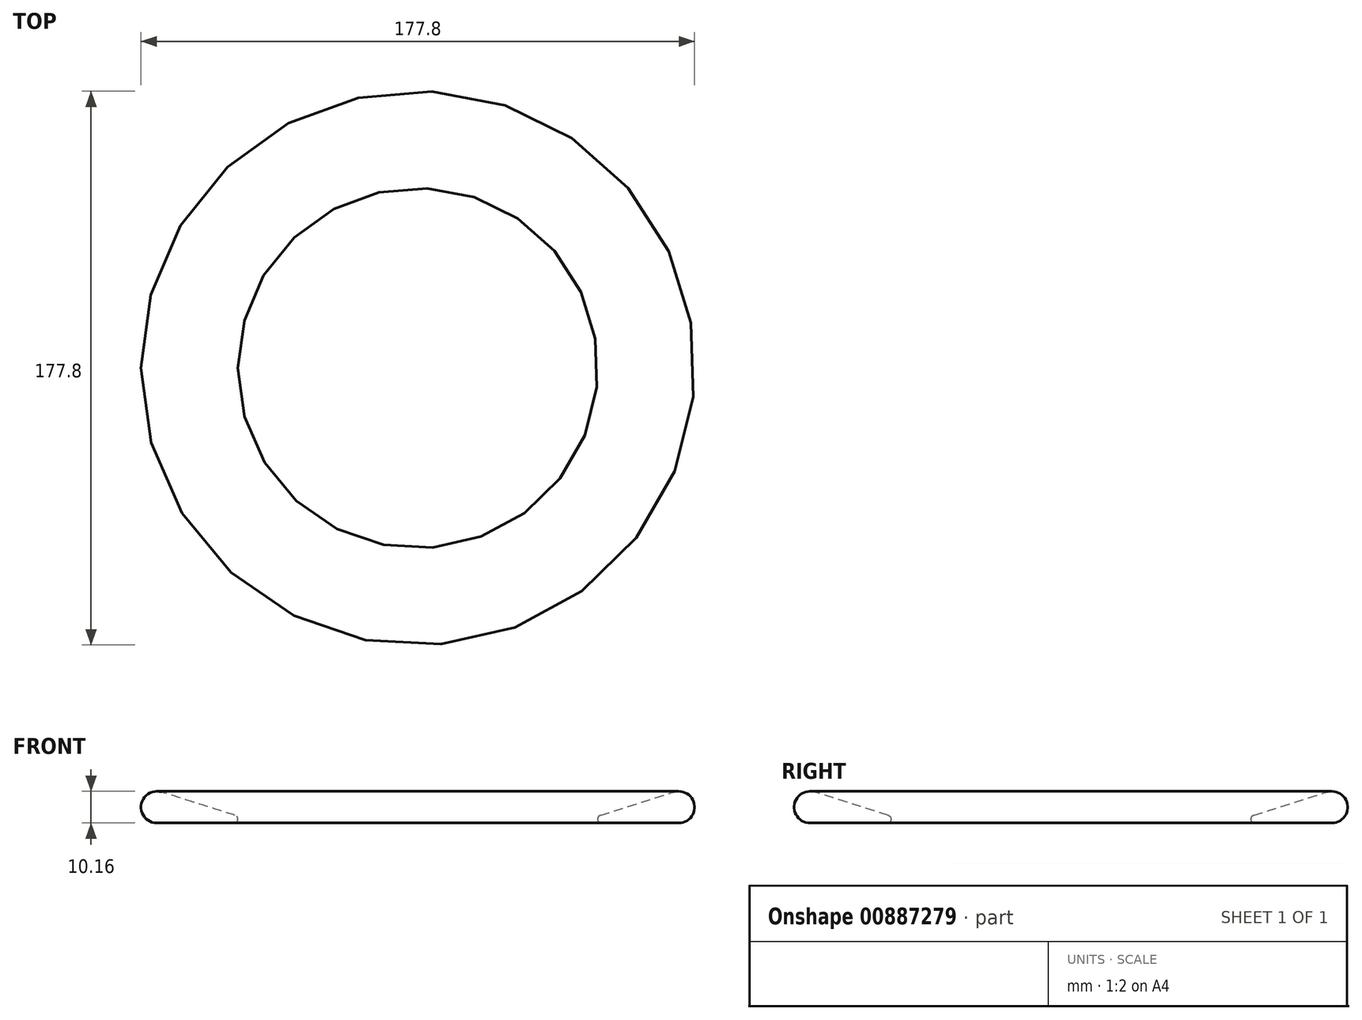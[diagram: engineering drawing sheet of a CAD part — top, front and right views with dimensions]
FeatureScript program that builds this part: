
annotation { "Feature Type Name" : "Feature", "Feature Type Description" : "" }
export const myFeature = defineFeature(function(context is Context, id is Id, definition is map)
    precondition{}
    {
        {
            var Q0;
            Q0=qCreatedBy(makeId("Front.planeOp"),FACE);
            var sketch = newSketch(context, id + "F0", { "sketchPlane" : qUnion([Q0])});
            skLineSegment(sketch, "E0", {"start": v(0, 0) * mm, "end": v(-50.8, 0) * mm});
            skLineSegment(sketch, "E1", {"start": v(-59.06, 0) * mm, "end": v(-83.82, 0) * mm});
            skArc(sketch, "E2", {"start": v(-83.82, 0) * mm, "mid": v(-88.84, 5.85) * mm, "end": v(-82.3, 9.93) * mm});
            skLineSegment(sketch, "E3", {"start": v(-82.3, 9.93) * mm, "end": v(-58.67, 2.48) * mm});
            skLineSegment(sketch, "E4", {"start": v(-88.9, 10.16) * mm, "end": v(-83.82, 10.16) * mm});
            skLineSegment(sketch, "E5", {"start": v(-88.9, 5.08) * mm, "end": v(-88.9, 0) * mm});
            skLineSegment(sketch, "E6", {"start": v(0, 0) * mm, "end": v(50.8, 0) * mm});
            skLineSegment(sketch, "E7", {"start": v(0, 0) * mm, "end": v(0, 40.2) * mm});
            skPoint(sketch, "E8.visualSharp", {"position": v(-50.8, 0) * mm});
            skArc(sketch, "E8.filletArc", {"start": v(-59.06, 0) * mm, "mid": v(-57.8, 1.08) * mm, "end": v(-58.67, 2.48) * mm});
            skSolve(sketch);
        }
        {
            var Q0;
            {var subQ4=sQuery(id+"F0.wireOp",EDGE,"E1");Q0=makeQuery(id+"F0.imprint","IMPRINT",FACE,{"disambiguationData":[TD([[makeQuery(id+"F0.imprint","IMPRINT",EDGE,{"derivedFrom":subQ4}),-1.0]])]});}
            var Q1;
            Q1=sQuery(id+"F0.wireOp",EDGE,"E7");
            revolve(context, id + "F1", {"surfaceOperationType" : NewSurfaceOperationType.NEW, "entities" : qUnion([Q0]), "axis" : qUnion([Q1]), "revolveType" : RevolveType.FULL});
        }
    });
